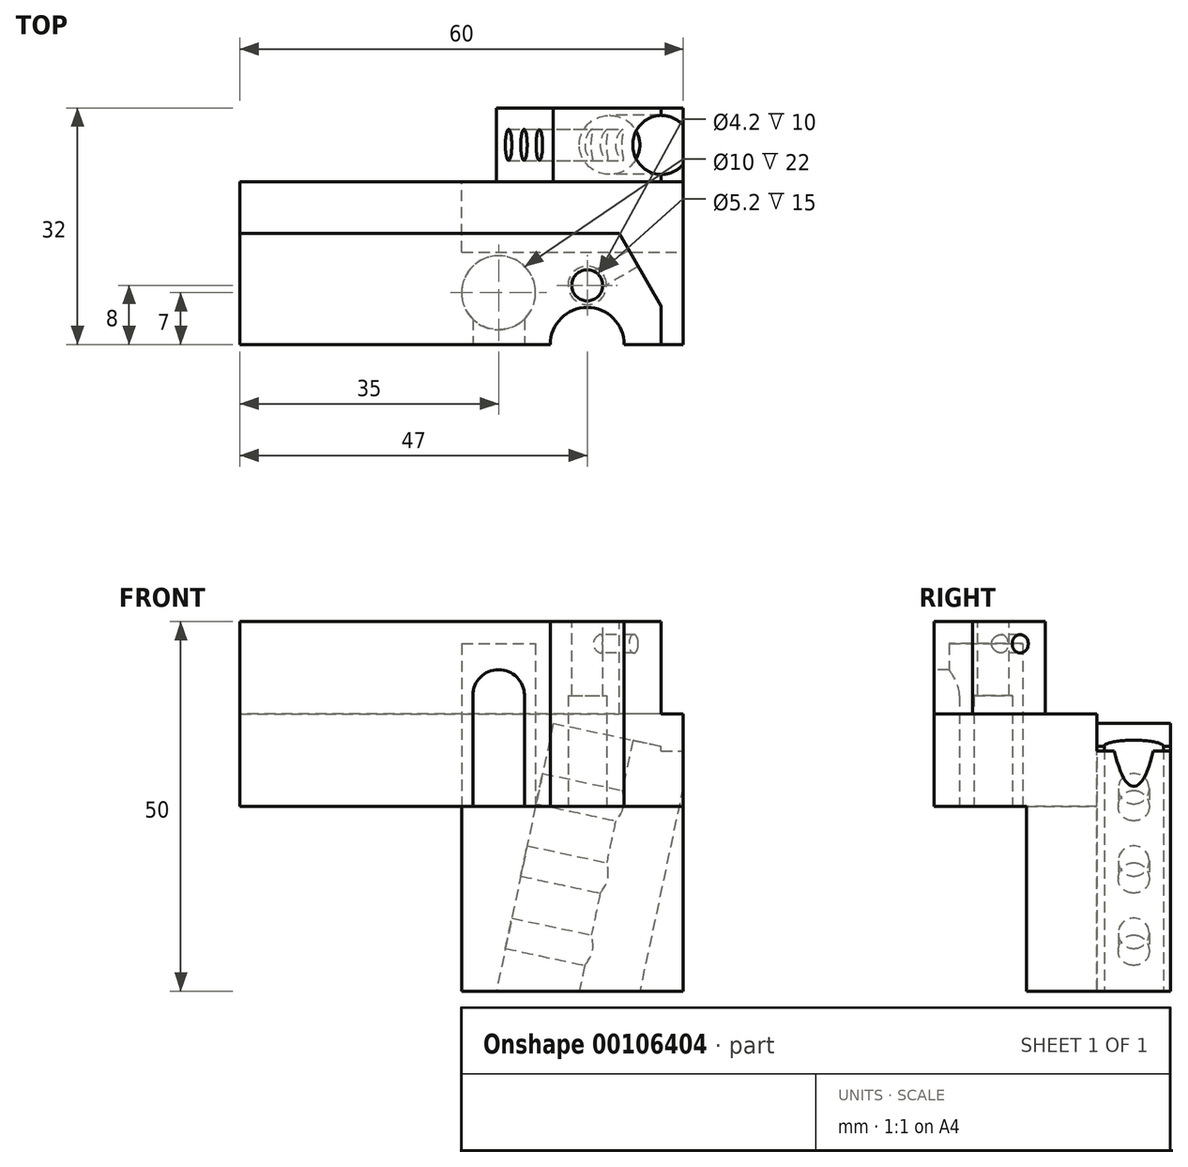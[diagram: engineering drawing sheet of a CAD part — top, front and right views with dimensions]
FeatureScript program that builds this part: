
annotation { "Feature Type Name" : "Feature", "Feature Type Description" : "" }
export const myFeature = defineFeature(function(context is Context, id is Id, definition is map)
    precondition{}
    {
        {
            var Q0;
            Q0=qCreatedBy(makeId("Right.planeOp"),FACE);
            var sketch = newSketch(context, id + "F0", { "sketchPlane" : qUnion([Q0])});
            skLineSegment(sketch, "E0.bottom", {"start": v(12.5, -12.5) * mm, "end": v(-12.5, -12.5) * mm});
            skLineSegment(sketch, "E0.top", {"start": v(12.5, 12.5) * mm, "end": v(-12.5, 12.5) * mm});
            skLineSegment(sketch, "E0.left", {"start": v(12.5, -12.5) * mm, "end": v(12.5, 12.5) * mm});
            skLineSegment(sketch, "E0.right", {"start": v(-12.5, -12.5) * mm, "end": v(-12.5, 12.5) * mm});
            skPoint(sketch, "E0.middle", {"position": v(0, 0) * mm});
            skSolve(sketch);
        }
        {
            var Q0;
            Q0=makeQuery(id+"F0.imprint","IMPRINT",FACE,{"disambiguationData":[TD([[makeQuery(id+"F0.imprint","IMPRINT",EDGE,{"derivedFrom":sQuery(id+"F0.wireOp",EDGE,"E0.bottom")}),-1.0]])]});
            extrude(context, id + "F1", {"entities" : qUnion([Q0]), "depth" : 60 * mm, "symmetric" : true});
        }
        {
            var Q0;
            Q0=makeQuery(id+"F1.opExtrude","SWEPT_FACE",FACE,{"disambiguationData":[OSD([sQuery(id+"F0.wireOp",EDGE,"E0.top")])]});
            var sketch = newSketch(context, id + "F2", { "sketchPlane" : qUnion([Q0])});
            skArc(sketch, "E1", {"start": v(22, -12.5) * mm, "mid": v(17, -7.5) * mm, "end": v(12, -12.5) * mm});
            skLineSegment(sketch, "E2", {"start": v(12, -12.5) * mm, "end": v(22, -12.5) * mm});
            skSolve(sketch);
        }
        {
            var Q0;
            Q0=makeQuery(id+"F2.imprint","IMPRINT",FACE,{"disambiguationData":[TD([[makeQuery(id+"F2.imprint","IMPRINT",EDGE,{"derivedFrom":sQuery(id+"F2.wireOp",EDGE,"E1")}),1.0]])]});
            extrude(context, id + "F3", {"entities" : qUnion([Q0]), "operationType" : NewBodyOperationType.REMOVE, "endBound" : BoundingType.THROUGH_ALL, "oppositeDirection" : true, "depth" : 25 * mm});
        }
        {
            var Q0;
            Q0=makeQuery(id+"F1.opExtrude","SWEPT_FACE",FACE,{"disambiguationData":[OSD([sQuery(id+"F0.wireOp",EDGE,"E0.top")])]});
            var sketch = newSketch(context, id + "F4", { "sketchPlane" : qUnion([Q0])});
            skCircle(sketch, "E3", {"center": v(17, -4.5) * mm, "radius": 2.1 * mm});
            skPoint(sketch, "E4", {"position": v(17, -7.5) * mm});
            skSolve(sketch);
        }
        {
            var Q0;
            Q0=makeQuery(id+"F4.imprint","IMPRINT",FACE,{"disambiguationData":[TD([[makeQuery(id+"F4.imprint","IMPRINT",EDGE,{"derivedFrom":sQuery(id+"F4.wireOp",EDGE,"E3")}),1.0]])]});
            extrude(context, id + "F5", {"entities" : qUnion([Q0]), "operationType" : NewBodyOperationType.REMOVE, "endBound" : BoundingType.THROUGH_ALL, "oppositeDirection" : true, "depth" : 25 * mm});
        }
        {
            var Q0;
            Q0=makeQuery(id+"F1.opExtrude","SWEPT_FACE",FACE,{"disambiguationData":[OSD([sQuery(id+"F0.wireOp",EDGE,"E0.bottom")])]});
            var sketch = newSketch(context, id + "F6", { "sketchPlane" : qUnion([Q0])});
            skCircle(sketch, "E5", {"center": v(5, 5.5) * mm, "radius": 5 * mm});
            skLineSegment(sketch, "E6", {"start": v(17, 12.5) * mm, "end": v(17, 0) * mm, "construction": true});
            skPoint(sketch, "E6.endSnap0", {"position": v(17, 7.5) * mm});
            skSolve(sketch);
        }
        {
            var Q0;
            Q0=makeQuery(id+"F6.imprint","IMPRINT",FACE,{"disambiguationData":[TD([[makeQuery(id+"F6.imprint","IMPRINT",EDGE,{"derivedFrom":sQuery(id+"F6.wireOp",EDGE,"E5")}),1.0]])]});
            extrude(context, id + "F7", {"entities" : qUnion([Q0]), "operationType" : NewBodyOperationType.REMOVE, "oppositeDirection" : true, "depth" : 22 * mm});
        }
        {
            var Q0;
            {var subQ0=sQuery(id+"F0.wireOp",EDGE,"E0.bottom");var subQ1=sQuery(id+"F0.wireOp",EDGE,"E0.right");var subQ2=sQuery(id+"F0.wireOp",EDGE,"E0.top");Q0=makeQuery(id+"F3.boolean.opBoolean","SPLIT",FACE,{"disambiguationData":[TD([makeQuery(id+"F1.opExtrude","CAP_FACE",FACE,{"disambiguationData":[OSD([subQ0,subQ2,sQuery(id+"F0.wireOp",EDGE,"E0.left"),subQ1])],"isStart":true})])],"derivedFrom":makeQuery(id+"F1.opExtrude","SWEPT_FACE",FACE,{"disambiguationData":[OSD([subQ1])]})});}
            var sketch = newSketch(context, id + "F8", { "sketchPlane" : qUnion([Q0])});
            skLineSegment(sketch, "E7", {"start": v(8.5, -12.5) * mm, "end": v(8.5, 2.5) * mm});
            skArc(sketch, "E8", {"start": v(8.5, 2.5) * mm, "mid": v(5, 6) * mm, "end": v(1.5, 2.5) * mm});
            skLineSegment(sketch, "E9", {"start": v(1.5, 2.5) * mm, "end": v(1.5, -12.5) * mm});
            skLineSegment(sketch, "E10", {"start": v(1.5, -12.5) * mm, "end": v(8.5, -12.5) * mm});
            skSolve(sketch);
        }
        {
            var Q0;
            Q0=makeQuery(id+"F8.imprint","IMPRINT",FACE,{"disambiguationData":[TD([[makeQuery(id+"F8.imprint","IMPRINT",EDGE,{"derivedFrom":sQuery(id+"F8.wireOp",EDGE,"E7")}),1.0]])]});
            extrude(context, id + "F9", {"entities" : qUnion([Q0]), "operationType" : NewBodyOperationType.REMOVE, "oppositeDirection" : true, "depth" : 7 * mm});
        }
        {
            var Q0;
            Q0=makeQuery(id+"F1.opExtrude","SWEPT_FACE",FACE,{"disambiguationData":[OSD([sQuery(id+"F0.wireOp",EDGE,"E0.bottom")])]});
            var sketch = newSketch(context, id + "F10", { "sketchPlane" : qUnion([Q0])});
            skCircle(sketch, "E11", {"center": v(17, 4.5) * mm, "radius": 2.6 * mm});
            skSolve(sketch);
        }
        {
            var Q0;
            Q0=qSketchRegion(id+"F10",true);
            extrude(context, id + "F11", {"entities" : qUnion([Q0]), "operationType" : NewBodyOperationType.REMOVE, "oppositeDirection" : true, "depth" : 15 * mm});
        }
        {
            var Q0;
            Q0=makeQuery(id+"F1.opExtrude","SWEPT_BODY",BODY,{"disambiguationData":[OSD([sQuery(id+"F0.wireOp",EDGE,"E0.bottom"),sQuery(id+"F0.wireOp",EDGE,"E0.top"),sQuery(id+"F0.wireOp",EDGE,"E0.left"),sQuery(id+"F0.wireOp",EDGE,"E0.right")])]});
            transform(context, id + "F12", {"entities" : qUnion([Q0]), "transformType" : TransformType.TRANSLATION_3D, "dx" : 0 * mm, "dy" : 0 * mm, "dz" : 0 * mm, "makeCopy" : true});
        }
        {
            var Q0;
            Q0=makeQuery(id+"F12.opPattern","COPY",BODY,{"derivedFrom":makeQuery(id+"F1.opExtrude","SWEPT_BODY",BODY,{"disambiguationData":[OSD([sQuery(id+"F0.wireOp",EDGE,"E0.bottom"),sQuery(id+"F0.wireOp",EDGE,"E0.top"),sQuery(id+"F0.wireOp",EDGE,"E0.left"),sQuery(id+"F0.wireOp",EDGE,"E0.right")])]}),"instanceName":"1"});
            deleteBodies(context, id + "F13", {"entities" : qUnion([Q0])});
        }
        {
            var Q0;
            Q0=makeQuery(id+"F1.opExtrude","SWEPT_FACE",FACE,{"disambiguationData":[OSD([sQuery(id+"F0.wireOp",EDGE,"E0.bottom")])]});
            var sketch = newSketch(context, id + "F14", { "sketchPlane" : qUnion([Q0])});
            skLineSegment(sketch, "E12.bottom", {"start": v(0, 0) * mm, "end": v(30, 0) * mm});
            skLineSegment(sketch, "E12.top", {"start": v(0, -12.5) * mm, "end": v(30, -12.5) * mm});
            skLineSegment(sketch, "E12.left", {"start": v(0, 0) * mm, "end": v(0, -12.5) * mm});
            skLineSegment(sketch, "E12.right", {"start": v(30, 0) * mm, "end": v(30, -12.5) * mm});
            skSolve(sketch);
        }
        {
            var Q0;
            Q0=makeQuery(id+"F14.imprint","IMPRINT",FACE,{"disambiguationData":[TD([[makeQuery(id+"F14.imprint","IMPRINT",EDGE,{"derivedFrom":sQuery(id+"F14.wireOp",EDGE,"E12.bottom")}),-1.0]])]});
            extrude(context, id + "F15", {"entities" : qUnion([Q0]), "operationType" : NewBodyOperationType.ADD, "depth" : 25 * mm});
        }
        {
            var Q0;
            Q0=makeQuery(id+"F15.boolean.opBoolean","MERGE",FACE,{"derivedFrom":[makeQuery(id+"F1.opExtrude","SWEPT_FACE",FACE,{"disambiguationData":[OSD([sQuery(id+"F0.wireOp",EDGE,"E0.left")])]}),makeQuery(id+"F15.opExtrude","SWEPT_FACE",FACE,{"disambiguationData":[OSD([sQuery(id+"F14.wireOp",EDGE,"E12.top")])]})]});
            extrude(context, id + "F16", {"entities" : qUnion([Q0]), "operationType" : NewBodyOperationType.ADD, "depth" : 7 * mm});
        }
        {
            var Q0;
            Q0=makeQuery(id+"F16.opExtrude","CAP_FACE",FACE,{"disambiguationData":[OSD([sQuery(id+"F0.wireOp",EDGE,"E0.left"),sQuery(id+"F14.wireOp",EDGE,"E12.top")])],"isStart":false});
            var sketch = newSketch(context, id + "F17", { "sketchPlane" : qUnion([Q0])});
            skLineSegment(sketch, "E13", {"start": v(-6.48, 0) * mm, "end": v(-30, -5) * mm});
            skLineSegment(sketch, "E14", {"start": v(-30, -5) * mm, "end": v(-30, 12.5) * mm});
            skLineSegment(sketch, "E15", {"start": v(-30, 12.5) * mm, "end": v(30, 12.5) * mm});
            skLineSegment(sketch, "E16", {"start": v(30, 12.5) * mm, "end": v(30, 0) * mm});
            skLineSegment(sketch, "E17", {"start": v(30, 0) * mm, "end": v(-6.48, 0) * mm});
            skSolve(sketch);
        }
        {
            var Q0;
            Q0=makeQuery(id+"F17.imprint","IMPRINT",FACE,{"disambiguationData":[TD([[makeQuery(id+"F17.imprint","IMPRINT",EDGE,{"derivedFrom":sQuery(id+"F17.wireOp",EDGE,"E13")}),-1.0]])]});
            extrude(context, id + "F18", {"entities" : qUnion([Q0]), "operationType" : NewBodyOperationType.REMOVE, "oppositeDirection" : true, "depth" : 10 * mm});
        }
        {
            var Q0;
            Q0=makeQuery(id+"F16.opExtrude","CAP_FACE",FACE,{"disambiguationData":[OSD([sQuery(id+"F0.wireOp",EDGE,"E0.left"),sQuery(id+"F14.wireOp",EDGE,"E12.top")])],"isStart":false});
            var sketch = newSketch(context, id + "F19", { "sketchPlane" : qUnion([Q0])});
            skLineSegment(sketch, "E18", {"start": v(-12.4, -1.26) * mm, "end": v(0, -59.56) * mm});
            skLineSegment(sketch, "E19", {"start": v(0, -59.56) * mm, "end": v(30, -59.56) * mm});
            skLineSegment(sketch, "E20", {"start": v(30, -59.56) * mm, "end": v(30, -1.26) * mm});
            skLineSegment(sketch, "E21", {"start": v(30, -1.26) * mm, "end": v(-12.4, -1.26) * mm});
            skLineSegment(sketch, "E22", {"start": v(-12.4, -1.26) * mm, "end": v(-12.4, 5.67) * mm});
            skLineSegment(sketch, "E23", {"start": v(-12.4, 5.67) * mm, "end": v(30, 5.67) * mm});
            skLineSegment(sketch, "E24", {"start": v(30, 5.67) * mm, "end": v(30, -1.26) * mm});
            skSolve(sketch);
        }
        {
            var Q0;
            {var subQ4=sQuery(id+"F19.wireOp",EDGE,"E21");Q0=makeQuery(id+"F19.imprint","IMPRINT",FACE,{"disambiguationData":[TD([[makeQuery(id+"F19.imprint","IMPRINT",EDGE,{"derivedFrom":subQ4}),1.0]])]});}
            var Q1;
            {var subQ3=sQuery(id+"F19.wireOp",EDGE,"E22");Q1=makeQuery(id+"F19.imprint","IMPRINT",FACE,{"disambiguationData":[TD([[makeQuery(id+"F19.imprint","IMPRINT",EDGE,{"derivedFrom":subQ3}),-1.0]])]});}
            var Q2;
            {var subQ0=sQuery(id+"F19.wireOp",EDGE,"E21");Q2=makeQuery(id+"F19.imprint","IMPRINT",FACE,{"disambiguationData":[TD([[makeQuery(id+"F19.imprint","IMPRINT",EDGE,{"derivedFrom":subQ0}),-1.0]])]});}
            extrude(context, id + "F20", {"entities" : qUnion([Q0, Q1, Q2]), "operationType" : NewBodyOperationType.REMOVE, "oppositeDirection" : true, "depth" : 10 * mm});
        }
        {
            var Q0;
            Q0=makeQuery(id+"F18.boolean.opBoolean","COPY",FACE,{"derivedFrom":makeQuery(id+"F18.opExtrude","SWEPT_FACE",FACE,{"disambiguationData":[OSD([sQuery(id+"F17.wireOp",EDGE,"E13")])]})});
            var sketch = newSketch(context, id + "F21", { "sketchPlane" : qUnion([Q0])});
            skLineSegment(sketch, "E25", {"start": v(27.38, 19.5) * mm, "end": v(27.38, 9.5) * mm, "construction": true});
            skPoint(sketch, "E26", {"position": v(27.38, 14.5) * mm});
            skSolve(sketch);
        }
        {
            var Q0;
            Q0=sQuery(id+"F21.wireOp",VERTEX,"E26");
            var Q1;
            Q1=makeQuery(id+"F1.opExtrude","SWEPT_BODY",BODY,{"disambiguationData":[OSD([sQuery(id+"F0.wireOp",EDGE,"E0.bottom"),sQuery(id+"F0.wireOp",EDGE,"E0.top"),sQuery(id+"F0.wireOp",EDGE,"E0.left"),sQuery(id+"F0.wireOp",EDGE,"E0.right")])]});
            var Q2;
            Q2=makeQuery(id+"F1.opExtrude","SWEPT_BODY",BODY,{"disambiguationData":[OSD([sQuery(id+"F0.wireOp",EDGE,"E0.bottom"),sQuery(id+"F0.wireOp",EDGE,"E0.top"),sQuery(id+"F0.wireOp",EDGE,"E0.left"),sQuery(id+"F0.wireOp",EDGE,"E0.right")])]});
            hole(context, id + "F22", {"style" : HoleStyle.SIMPLE, "endStyle" : HoleEndStyle.THROUGH, "standardTappedOrClearance" : lookupTablePath({ "standard" : "ISO", "size" : "8", "type" : "Drilled" }), "standardBlindInLast" : lookupTablePath({ "standard" : "ISO", "size" : "8", "type" : "Drilled" }), "holeDiameter" : 8 * mm, "locations" : qUnion([Q0]), "scope" : qUnion([Q1, Q2]), "isTappedThrough" : true, "startStyle" : HoleStartStyle.SKETCH});
        }
        {
            var Q0;
            {var subQ0=sQuery(id+"F0.wireOp",EDGE,"E0.top");Q0=makeQuery(id+"F16.boolean.opBoolean","MERGE",FACE,{"derivedFrom":[makeQuery(id+"F1.opExtrude","SWEPT_FACE",FACE,{"disambiguationData":[OSD([subQ0])]}),makeQuery(id+"F16.opExtrude","SWEPT_FACE",FACE,{"disambiguationData":[OSD([subQ0,sQuery(id+"F0.wireOp",EDGE,"E0.left")])]})]});}
            var sketch = newSketch(context, id + "F23", { "sketchPlane" : qUnion([Q0])});
            skLineSegment(sketch, "E27", {"start": v(30, -12.5) * mm, "end": v(17.3, 9.5) * mm});
            skLineSegment(sketch, "E28", {"start": v(17.3, 9.5) * mm, "end": v(30, 9.5) * mm});
            skLineSegment(sketch, "E29", {"start": v(30, 9.5) * mm, "end": v(30, -12.5) * mm});
            skLineSegment(sketch, "E30", {"start": v(-30.04, 2.5) * mm, "end": v(21.34, 2.5) * mm});
            skLineSegment(sketch, "E31", {"start": v(-30.04, 2.5) * mm, "end": v(-30, 9.5) * mm});
            skLineSegment(sketch, "E32", {"start": v(-30, 9.5) * mm, "end": v(17.3, 9.5) * mm});
            skSolve(sketch);
        }
        {
            var Q0;
            Q0=makeQuery(id+"F23.imprint","IMPRINT",FACE,{"disambiguationData":[TD([[makeQuery(id+"F23.imprint","IMPRINT",EDGE,{"derivedFrom":sQuery(id+"F23.wireOp",EDGE,"E27")}),-1.0]])]});
            var Q1;
            {var subQ0=sQuery(id+"F23.wireOp",EDGE,"E32");Q1=makeQuery(id+"F23.imprint","IMPRINT",FACE,{"disambiguationData":[TD([[makeQuery(id+"F23.imprint","IMPRINT",EDGE,{"derivedFrom":subQ0}),1.0]])]});}
            extrude(context, id + "F24", {"entities" : qUnion([Q0, Q1]), "operationType" : NewBodyOperationType.REMOVE, "oppositeDirection" : true, "depth" : 12.5 * mm});
        }
        {
            var Q0;
            {var subQ0=sQuery(id+"F14.wireOp",EDGE,"E12.right");var subQ1=sQuery(id+"F0.wireOp",EDGE,"E0.left");Q0=makeQuery(id+"F16.boolean.opBoolean","MERGE",FACE,{"derivedFrom":[makeQuery(id+"F15.boolean.opBoolean","MERGE",FACE,{"derivedFrom":[makeQuery(id+"F1.opExtrude","CAP_FACE",FACE,{"disambiguationData":[OSD([sQuery(id+"F0.wireOp",EDGE,"E0.bottom"),sQuery(id+"F0.wireOp",EDGE,"E0.top"),subQ1,sQuery(id+"F0.wireOp",EDGE,"E0.right")])],"isStart":false}),makeQuery(id+"F15.opExtrude","SWEPT_FACE",FACE,{"disambiguationData":[OSD([subQ0])]})]}),makeQuery(id+"F16.opExtrude","SWEPT_FACE",FACE,{"disambiguationData":[OSD([subQ1,sQuery(id+"F14.wireOp",EDGE,"E12.top"),subQ0])]})]});}
            var sketch = newSketch(context, id + "F25", { "sketchPlane" : qUnion([Q0])});
            skLineSegment(sketch, "E33.bottom", {"start": v(-12.5, -12.5) * mm, "end": v(19.5, -12.5) * mm});
            skLineSegment(sketch, "E33.top", {"start": v(-12.5, 12.5) * mm, "end": v(19.5, 12.5) * mm});
            skLineSegment(sketch, "E33.left", {"start": v(-12.5, -12.5) * mm, "end": v(-12.5, 12.5) * mm});
            skLineSegment(sketch, "E33.right", {"start": v(19.5, -12.5) * mm, "end": v(19.5, 12.5) * mm});
            skPoint(sketch, "E34.oppositeSnap0", {"position": v(9.75, -37.5) * mm});
            skLineSegment(sketch, "E34.bottom", {"start": v(0, -12.5) * mm, "end": v(9.5, -12.5) * mm});
            skLineSegment(sketch, "E34.top", {"start": v(0, -37.5) * mm, "end": v(9.5, -37.5) * mm});
            skLineSegment(sketch, "E34.left", {"start": v(0, -12.5) * mm, "end": v(0, -37.5) * mm});
            skLineSegment(sketch, "E34.right", {"start": v(9.5, -12.5) * mm, "end": v(9.5, -37.5) * mm});
            skSolve(sketch);
        }
        {
            var Q0;
            {var subQ3=makeQuery(id+"F24.boolean.opBoolean","COPY",EDGE,{"derivedFrom":makeQuery(id+"F24.opExtrude","CAP_EDGE",EDGE,{"disambiguationData":[OSD([sQuery(id+"F23.wireOp",EDGE,"E29")])],"isStart":false})});Q0=makeQuery(id+"F25.imprint","IMPRINT",FACE,{"disambiguationData":[TD([[makeQuery(id+"F25.imprint","IMPRINT",EDGE,{"derivedFrom":subQ3}),1.0]])]});}
            var Q1;
            {var subQ2=sQuery(id+"F25.wireOp",EDGE,"E33.top");Q1=makeQuery(id+"F25.imprint","IMPRINT",FACE,{"disambiguationData":[TD([[makeQuery(id+"F25.imprint","IMPRINT",EDGE,{"derivedFrom":subQ2}),-1.0]])]});}
            var Q2;
            Q2=makeQuery(id+"F25.imprint","IMPRINT",FACE,{"disambiguationData":[TD([[makeQuery(id+"F25.imprint","IMPRINT",EDGE,{"derivedFrom":sQuery(id+"F25.wireOp",EDGE,"E34.bottom")}),-1.0]])]});
            extrude(context, id + "F26", {"entities" : qUnion([Q0, Q1, Q2]), "operationType" : NewBodyOperationType.REMOVE, "oppositeDirection" : true, "depth" : 3 * mm});
        }
        {
            var Q0;
            Q0=makeQuery(id+"F20.boolean.opBoolean","COPY",FACE,{"derivedFrom":makeQuery(id+"F20.opExtrude","SWEPT_FACE",FACE,{"disambiguationData":[OSD([sQuery(id+"F19.wireOp",EDGE,"E18")])]})});
            var sketch = newSketch(context, id + "F27", { "sketchPlane" : qUnion([Q0])});
            skLineSegment(sketch, "E35", {"start": v(-14.5, 1.35) * mm, "end": v(-14.5, -35.7) * mm, "construction": true});
            skPoint(sketch, "E36", {"position": v(-14.5, -7.7) * mm});
            skPoint(sketch, "E37", {"position": v(-14.5, -17.7) * mm});
            skPoint(sketch, "E38", {"position": v(-14.5, -27.7) * mm});
            skSolve(sketch);
        }
        {
            var Q0;
            Q0=sQuery(id+"F27.wireOp",VERTEX,"E36");
            var Q1;
            Q1=sQuery(id+"F27.wireOp",VERTEX,"E37");
            var Q2;
            Q2=sQuery(id+"F27.wireOp",VERTEX,"E38");
            var Q3;
            Q3=makeQuery(id+"F1.opExtrude","SWEPT_BODY",BODY,{"disambiguationData":[OSD([sQuery(id+"F0.wireOp",EDGE,"E0.bottom"),sQuery(id+"F0.wireOp",EDGE,"E0.top"),sQuery(id+"F0.wireOp",EDGE,"E0.left"),sQuery(id+"F0.wireOp",EDGE,"E0.right")])]});
            var Q4;
            Q4=makeQuery(id+"F1.opExtrude","SWEPT_BODY",BODY,{"disambiguationData":[OSD([sQuery(id+"F0.wireOp",EDGE,"E0.bottom"),sQuery(id+"F0.wireOp",EDGE,"E0.top"),sQuery(id+"F0.wireOp",EDGE,"E0.left"),sQuery(id+"F0.wireOp",EDGE,"E0.right")])]});
            hole(context, id + "F28", {"style" : HoleStyle.SIMPLE, "endStyle" : HoleEndStyle.BLIND, "standardTappedOrClearance" : lookupTablePath({ "standard" : "ISO", "engagement" : "75%", "pitch" : "0.8 mm", "size" : "M5", "type" : "Tapped" }), "standardBlindInLast" : lookupTablePath({ "standard" : "ISO", "engagement" : "75%", "pitch" : "0.8 mm", "size" : "M5", "type" : "Tapped" }), "holeDiameter" : 4.2 * mm, "holeDepth" : 15 * mm, "locations" : qUnion([Q0, Q1, Q2]), "scope" : qUnion([Q3, Q4]), "majorDiameter" : 5 * mm, "startStyle" : HoleStartStyle.SKETCH});
        }
        {
            var Q0;
            {var subQ0=sQuery(id+"F0.wireOp",EDGE,"E0.top");Q0=makeQuery(id+"F16.boolean.opBoolean","MERGE",FACE,{"derivedFrom":[makeQuery(id+"F1.opExtrude","SWEPT_FACE",FACE,{"disambiguationData":[OSD([subQ0])]}),makeQuery(id+"F16.opExtrude","SWEPT_FACE",FACE,{"disambiguationData":[OSD([subQ0,sQuery(id+"F0.wireOp",EDGE,"E0.left")])]})]});}
            var sketch = newSketch(context, id + "F29", { "sketchPlane" : qUnion([Q0])});
            skLineSegment(sketch, "E39", {"start": v(18.82, -3.45) * mm, "end": v(23.29, -0.87) * mm, "construction": true});
            skPoint(sketch, "E40", {"position": v(23.29, -0.87) * mm});
            skSolve(sketch);
        }
        {
            var Q0;
            Q0=makeQuery(id+"F24.boolean.opBoolean","COPY",FACE,{"derivedFrom":makeQuery(id+"F24.opExtrude","SWEPT_FACE",FACE,{"disambiguationData":[OSD([sQuery(id+"F23.wireOp",EDGE,"E27")])]})});
            var sketch = newSketch(context, id + "F30", { "sketchPlane" : qUnion([Q0])});
            skPoint(sketch, "E41", {"position": v(-12.4, 9.5) * mm});
            skSolve(sketch);
        }
        {
            var Q0;
            Q0=sQuery(id+"F30.wireOp",VERTEX,"E41");
            var Q1;
            Q1=makeQuery(id+"F1.opExtrude","SWEPT_BODY",BODY,{"disambiguationData":[OSD([sQuery(id+"F0.wireOp",EDGE,"E0.bottom"),sQuery(id+"F0.wireOp",EDGE,"E0.top"),sQuery(id+"F0.wireOp",EDGE,"E0.left"),sQuery(id+"F0.wireOp",EDGE,"E0.right")])]});
            hole(context, id + "F31", {"style" : HoleStyle.SIMPLE, "endStyle" : HoleEndStyle.BLIND, "standardTappedOrClearance" : lookupTablePath({ "standard" : "ISO", "engagement" : "75%", "pitch" : "0.5 mm", "size" : "M3", "type" : "Tapped" }), "standardBlindInLast" : lookupTablePath({ "standard" : "ISO", "engagement" : "75%", "pitch" : "0.5 mm", "size" : "M3", "type" : "Tapped" }), "holeDiameter" : 2.5 * mm, "holeDepth" : 8 * mm, "locations" : qUnion([Q0]), "scope" : qUnion([Q1]), "majorDiameter" : 3 * mm, "startStyle" : HoleStartStyle.SKETCH});
        }
    });
